# Revit family: Door_Sliding-Bypass_5Lite-Frosted
name_source: partatom
category: Doors
units: mm (PartAtom-declared; Revit-internal decimal feet)

## family parameters
Always vertical = Yes
Classification Number = 23.30.10.17.11
Cut with Voids When Loaded = No
Host = Wall
Room Calculation Point = No
Shared = No

## types (1)
- 2240
    3Pnl = No
    4pnl = No
    Assembly Code = C1020110
    Description = Sliding Bypass Door as Specified
    Exterior Trim = Wood_Pine_Painted-Color as Specified
    Floor Gap = 0' - 0 3/4"
    Frame Finish = Wood - Renin - Espresso
    Frame Projection Ext. = 0' - 1"
    Frame Projection Int. = 0' - 1"
    Frame Width = 0' - 3"
    Function = Interior
    Head Gap = 0' - 1"
    Height = 7' - 0"
    Interior Trim = Wood_Pine_Painted-Color as Specified
    Jamb Material = Wood_Pine_Painted-Color as Specified
    Keynote = 08 32 13
    Manufacturer = Renin Canada Corp.
    Manufacturer Fax = 905-791-3813
    Manufacturer Website = http://www.eriashomedesigns.com
    Model = 2240
    Operation = Sliding
    Panel = Panel_5Lite : Panel
    Panel Count = 2
    Panel Finish = Glass_Tempered_Frosted
    Panel Thickness = 0' - 0 1/4"
    Panel Width = 4' - 0"
    Product Data = http://www.arcat.com
    Revision = R1_01-2016
    Rough Height = 7' - 1"
    Rough Opening Gap = 0' - 0 1/4"
    Rough Width = 8' - 2"
    Sales Information = http://www.eriashomedesigns.com
    Show Trim = Yes
    Specification = http://www.arcat.com
    Stile Thickness = 0' - 2"
    Thickness = 0' - 1 3/8"
    Threshold Depth = 0' - 3 1/2"
    Threshold Finish = Wood - Renin - Espresso
    Total Opening Height = 7' - 1 3/4"
    Trim Reveal = 0' - 0 1/16"
    URL = http://www.eriashomedesigns.com
    Wall Closure = By host
    Width = 8' - 0"
    _Jamb Thickness = 0' - 0 3/4"
    spread = 0' - 1 9/16"

## geometry (parser evidence)
native form markers: Blend x22, Sweep x10
no freeform markers — native parametric forms only
